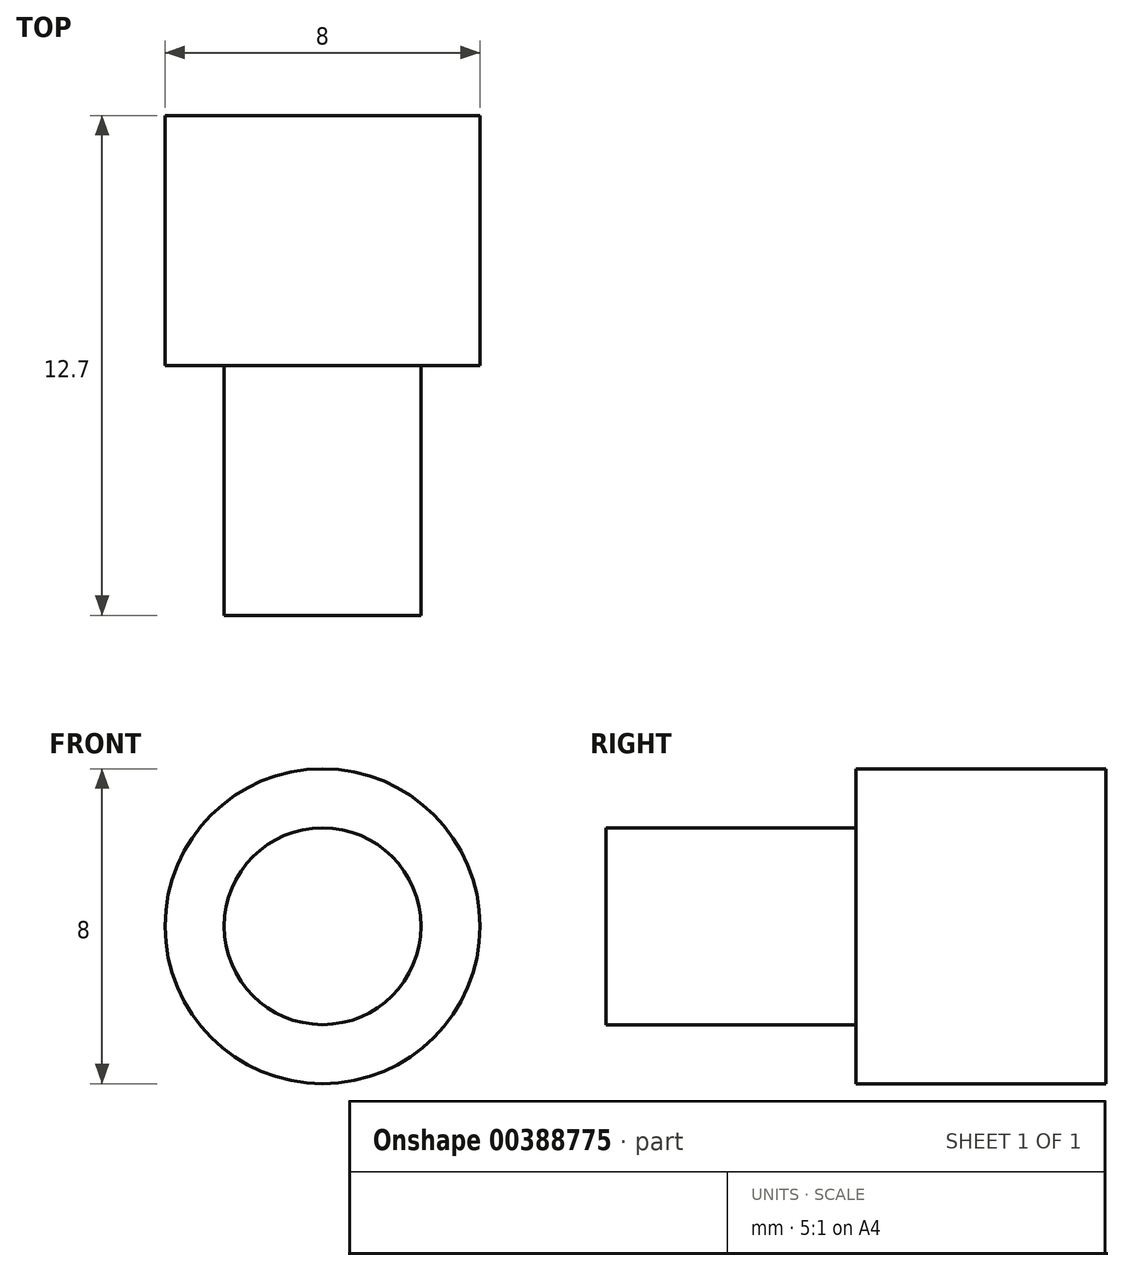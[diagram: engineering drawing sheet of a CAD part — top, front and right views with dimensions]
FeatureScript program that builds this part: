
annotation { "Feature Type Name" : "Feature", "Feature Type Description" : "" }
export const myFeature = defineFeature(function(context is Context, id is Id, definition is map)
    precondition{}
    {
        {
            var Q0;
            Q0=qCreatedBy(makeId("Front.planeOp"),FACE);
            var sketch = newSketch(context, id + "F0", { "sketchPlane" : qUnion([Q0])});
            skCircle(sketch, "E0", {"center": v(0, 0) * mm, "radius": 2.5 * mm});
            skCircle(sketch, "E1", {"center": v(0, 0) * mm, "radius": 4 * mm});
            skSolve(sketch);
        }
        {
            var Q0;
            Q0=makeQuery(id+"F0.imprint","IMPRINT",FACE,{"disambiguationData":[TD([[makeQuery(id+"F0.imprint","IMPRINT",EDGE,{"derivedFrom":sQuery(id+"F0.wireOp",EDGE,"E0")}),1.0]])]});
            extrude(context, id + "F1", {"entities" : qUnion([Q0]), "depth" : 6.35 * mm});
        }
        {
            var Q0;
            Q0=makeQuery(id+"F0.imprint","IMPRINT",FACE,{"disambiguationData":[TD([[makeQuery(id+"F0.imprint","IMPRINT",EDGE,{"derivedFrom":sQuery(id+"F0.wireOp",EDGE,"E0")}),-1.0]])]});
            var Q1;
            Q1=makeQuery(id+"F0.imprint","IMPRINT",FACE,{"disambiguationData":[TD([[makeQuery(id+"F0.imprint","IMPRINT",EDGE,{"derivedFrom":sQuery(id+"F0.wireOp",EDGE,"E0")}),1.0]])]});
            extrude(context, id + "F2", {"entities" : qUnion([Q0, Q1]), "oppositeDirection" : true, "depth" : 6.35 * mm});
        }
    });
